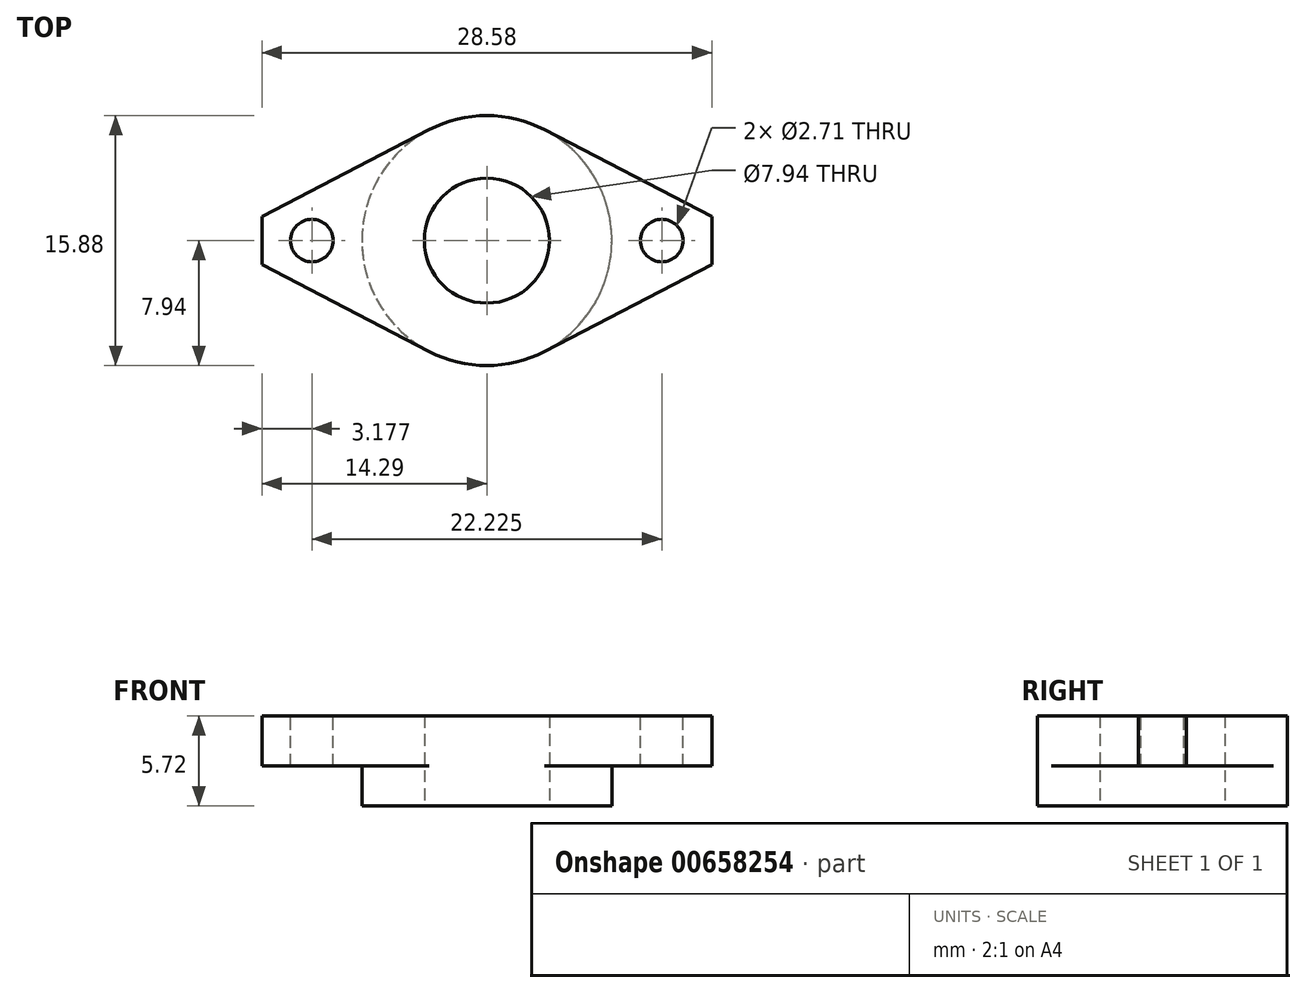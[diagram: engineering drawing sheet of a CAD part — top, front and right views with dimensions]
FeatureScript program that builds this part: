
annotation { "Feature Type Name" : "Feature", "Feature Type Description" : "" }
export const myFeature = defineFeature(function(context is Context, id is Id, definition is map)
    precondition{}
    {
        {
            var Q0;
            Q0=qCreatedBy(makeId("Top.planeOp"),FACE);
            var sketch = newSketch(context, id + "F0", { "sketchPlane" : qUnion([Q0])});
            skCircle(sketch, "E0", {"center": v(0, 0) * mm, "radius": 7.94 * mm});
            skCircle(sketch, "E1", {"center": v(0, 0) * mm, "radius": 3.97 * mm});
            skSolve(sketch);
        }
        {
            var Q0;
            Q0 = qSketchRegion(id + "F0", true);
            extrude(context, id + "F1", {"entities" : qUnion([Q0]), "depth" : 5.7 * mm, "offsetDistance" : 25.4 * mm});
        }
        {
            var Q0;
            Q0=makeQuery(id+"F1.opExtrude","CAP_FACE",FACE,{"disambiguationData":[OSD([sQuery(id+"F0.wireOp",EDGE,"E0"),sQuery(id+"F0.wireOp",EDGE,"E1")])],"isStart":false});
            var sketch = newSketch(context, id + "F2", { "sketchPlane" : qUnion([Q0])});
            skCircle(sketch, "E2", {"center": v(-11.11, 0) * mm, "radius": 1.35 * mm});
            skCircle(sketch, "E3", {"center": v(11.11, 0) * mm, "radius": 1.35 * mm});
            skLineSegment(sketch, "E4", {"start": v(-14.29, 1.53) * mm, "end": v(-14.29, -1.53) * mm});
            skLineSegment(sketch, "E5", {"start": v(14.29, 1.53) * mm, "end": v(14.29, -1.53) * mm});
            skPoint(sketch, "E6", {"position": v(3.66, 7.04) * mm});
            skPoint(sketch, "E7", {"position": v(14.29, 1.53) * mm});
            skPoint(sketch, "E8", {"position": v(14.29, -1.53) * mm});
            skPoint(sketch, "E9", {"position": v(3.66, -7.04) * mm});
            skLineSegment(sketch, "E10", {"start": v(3.66, 7.04) * mm, "end": v(14.29, 1.53) * mm});
            skLineSegment(sketch, "E11", {"start": v(3.66, -7.04) * mm, "end": v(14.29, -1.53) * mm});
            skPoint(sketch, "E12", {"position": v(-14.29, 1.53) * mm});
            skPoint(sketch, "E13", {"position": v(-14.29, -1.53) * mm});
            skPoint(sketch, "E14", {"position": v(-3.66, -7.04) * mm});
            skPoint(sketch, "E15", {"position": v(-3.66, 7.04) * mm});
            skLineSegment(sketch, "E16", {"start": v(-3.66, 7.04) * mm, "end": v(-14.29, 1.53) * mm});
            skLineSegment(sketch, "E17", {"start": v(-14.29, -1.53) * mm, "end": v(-3.66, -7.04) * mm});
            skSolve(sketch);
        }
        {
            var Q0;
            Q0=makeQuery(id+"F2.imprint","IMPRINT",FACE,{"disambiguationData":[TD([[makeQuery(id+"F2.imprint","IMPRINT",EDGE,{"derivedFrom":sQuery(id+"F2.wireOp",EDGE,"E2")}),-1.0]])]});
            var Q1;
            Q1=makeQuery(id+"F2.imprint","IMPRINT",FACE,{"disambiguationData":[TD([[makeQuery(id+"F2.imprint","IMPRINT",EDGE,{"derivedFrom":sQuery(id+"F2.wireOp",EDGE,"E3")}),-1.0]])]});
            extrude(context, id + "F3", {"entities" : qUnion([Q0, Q1]), "operationType" : NewBodyOperationType.ADD, "oppositeDirection" : true, "depth" : 3.17 * mm, "offsetDistance" : 25.4 * mm});
        }
    });
